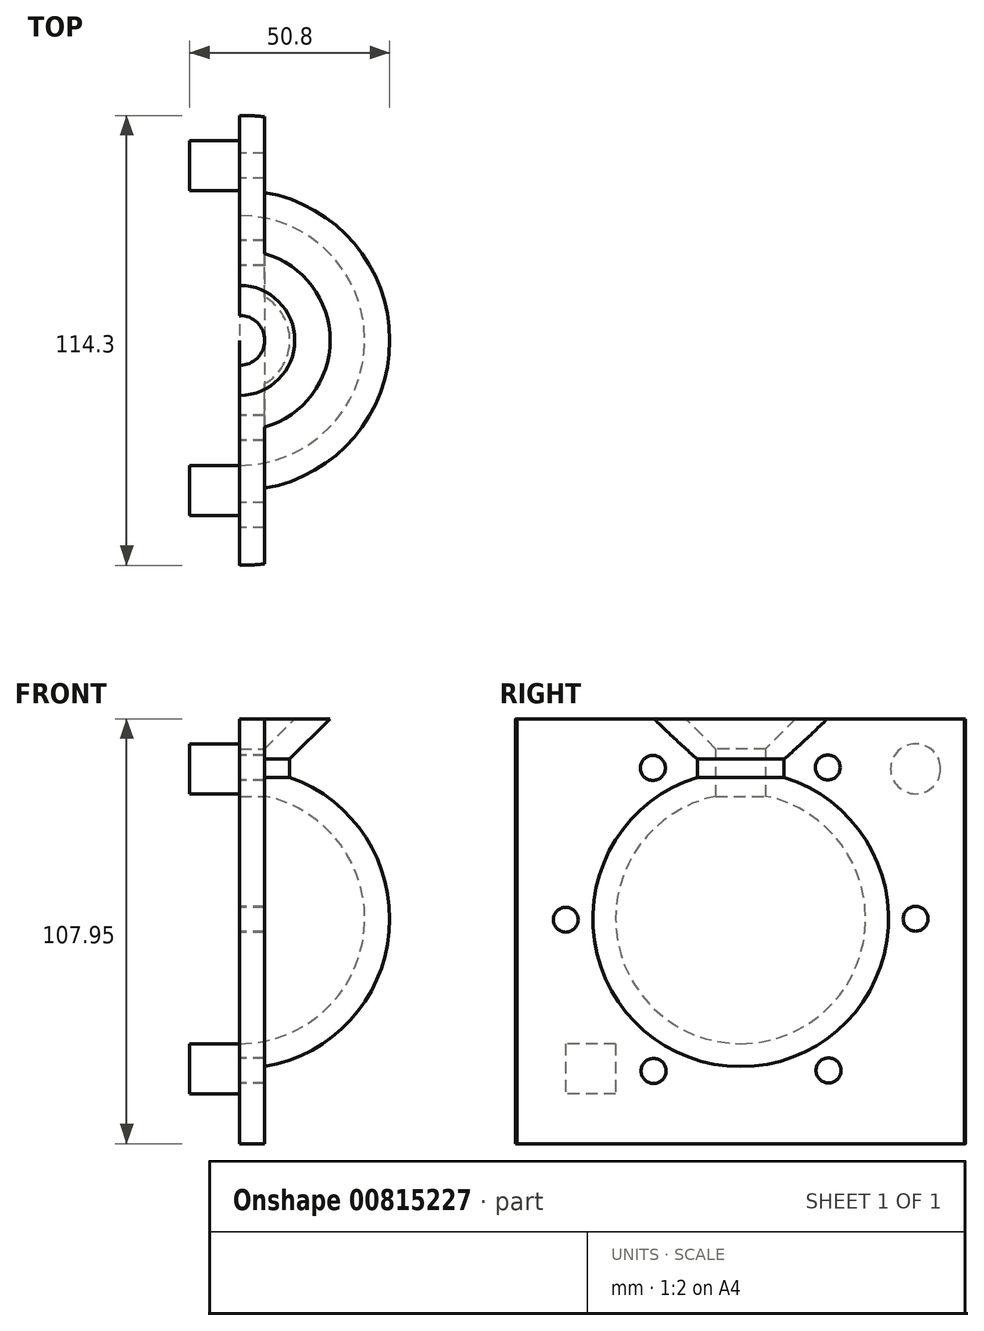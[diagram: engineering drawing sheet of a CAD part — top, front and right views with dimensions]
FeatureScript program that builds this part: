
annotation { "Feature Type Name" : "Feature", "Feature Type Description" : "" }
export const myFeature = defineFeature(function(context is Context, id is Id, definition is map)
    precondition{}
    {
        {
            var Q0;
            Q0=qCreatedBy(makeId("Right.planeOp"),FACE);
            var sketch = newSketch(context, id + "F0", { "sketchPlane" : qUnion([Q0])});
            skCircle(sketch, "E0", {"center": v(0, 0) * mm, "radius": 31.75 * mm});
            skLineSegment(sketch, "E1", {"start": v(0, -31.75) * mm, "end": v(0, -57.15) * mm});
            skLineSegment(sketch, "E2", {"start": v(0, -57.15) * mm, "end": v(57.15, -57.15) * mm});
            skLineSegment(sketch, "E3", {"start": v(57.15, -57.15) * mm, "end": v(57.15, 50.8) * mm});
            skLineSegment(sketch, "E4", {"start": v(57.15, 50.8) * mm, "end": v(6.35, 50.8) * mm});
            skLineSegment(sketch, "E5", {"start": v(6.35, 50.8) * mm, "end": v(6.35, 31.1) * mm});
            skSolve(sketch);
        }
        {
            var Q0;
            {var subQ0=sQuery(id+"F0.wireOp",EDGE,"E1");Q0=makeQuery(id+"F0.imprint","IMPRINT",FACE,{"disambiguationData":[TD([[makeQuery(id+"F0.imprint","IMPRINT",EDGE,{"derivedFrom":subQ0}),1.0]])]});}
            var Q1;
            Q1=sQuery(id+"F0.wireOp",EDGE,"E1");
            revolve(context, id + "F1", {"surfaceOperationType" : NewSurfaceOperationType.NEW, "entities" : qUnion([Q0]), "axis" : qUnion([Q1]), "revolveType" : RevolveType.ONE_DIRECTION, "angle" : 180 * degree});
        }
        {
            var Q0;
            Q0=makeQuery(id+"F1.opRevolve","CAP_FACE",FACE,{"disambiguationData":[OSD([sQuery(id+"F0.wireOp",EDGE,"E0"),sQuery(id+"F0.wireOp",EDGE,"E1"),sQuery(id+"F0.wireOp",EDGE,"E2"),sQuery(id+"F0.wireOp",EDGE,"E3"),sQuery(id+"F0.wireOp",EDGE,"E4"),sQuery(id+"F0.wireOp",EDGE,"E5")])],"isStart":false});
            var sketch = newSketch(context, id + "F2", { "sketchPlane" : qUnion([Q0])});
            skCircle(sketch, "E6", {"center": v(-44.45, 38.1) * mm, "radius": 6.35 * mm});
            skLineSegment(sketch, "E7.bottom", {"start": v(31.75, -31.75) * mm, "end": v(44.45, -31.75) * mm});
            skLineSegment(sketch, "E7.top", {"start": v(31.75, -44.45) * mm, "end": v(44.45, -44.45) * mm});
            skLineSegment(sketch, "E7.left", {"start": v(31.75, -31.75) * mm, "end": v(31.75, -44.45) * mm});
            skLineSegment(sketch, "E7.right", {"start": v(44.45, -31.75) * mm, "end": v(44.45, -44.45) * mm});
            skSolve(sketch);
        }
        {
            var Q0;
            Q0=qSketchRegion(id+"F2",true);
            extrude(context, id + "F3", {"entities" : qUnion([Q0]), "operationType" : NewBodyOperationType.ADD, "depth" : 12.7 * mm, "offsetDistance" : 25.4 * mm});
        }
        {
            var Q0;
            Q0=makeQuery(id+"F1.opRevolve","SWEPT_EDGE",EDGE,{"disambiguationData":[OSD([sQuery(id+"F0.wireOp",EDGE,"E4"),sQuery(id+"F0.wireOp",EDGE,"E5")])]});
            chamfer(context, id + "F4", {"entities" : qUnion([Q0]), "width" : 7.62 * mm, "tangentPropagation" : true});
        }
        {
            var Q0;
            Q0=makeQuery(id+"F1.opRevolve","SWEPT_FACE",FACE,{"disambiguationData":[OSD([sQuery(id+"F0.wireOp",EDGE,"E4")])]});
            var Q1;
            Q1=makeQuery(id+"F1.opRevolve","SWEPT_FACE",FACE,{"disambiguationData":[OSD([sQuery(id+"F0.wireOp",EDGE,"E3")])]});
            var Q2;
            Q2=makeQuery(id+"F1.opRevolve","SWEPT_FACE",FACE,{"disambiguationData":[OSD([sQuery(id+"F0.wireOp",EDGE,"E2")])]});
            shell(context, id + "F5", {"entities" : qUnion([Q0, Q1, Q2]), "thickness" : 6.35 * mm});
        }
        {
            var Q0;
            {var subQ0=sQuery(id+"F0.wireOp",EDGE,"E0");var subQ1=makeQuery(id+"F0.imprint","INTERSECT",VERTEX,{"derivedFrom":[subQ0,sQuery(id+"F0.wireOp",EDGE,"E1")]});Q0=makeQuery(id+"F0.imprint","IMPRINT",FACE,{"disambiguationData":[TD([[makeQuery(id+"F0.imprint","IMPRINT",EDGE,{"disambiguationData":[TD([[subQ1,1.0]])],"derivedFrom":subQ0}),1.0]])]});}
            var sketch = newSketch(context, id + "F6", { "sketchPlane" : qUnion([Q0])});
            skArc(sketch, "E8", {"start": v(24.87, 36.84) * mm, "mid": v(22.18, 38.52) * mm, "end": v(19.37, 40) * mm});
            skCircle(sketch, "E9", {"center": v(44.45, 0) * mm, "radius": 3.18 * mm});
            skCircle(sketch, "E10.1.0", {"center": v(22.12, 38.43) * mm, "radius": 3.18 * mm});
            skCircle(sketch, "E10.2.0", {"center": v(-22.32, 38.3) * mm, "radius": 3.18 * mm});
            skCircle(sketch, "E10.3.0", {"center": v(-44.44, -0.24) * mm, "radius": 3.18 * mm});
            skCircle(sketch, "E10.4.0", {"center": v(-22.11, -38.67) * mm, "radius": 3.18 * mm});
            skCircle(sketch, "E10.5.0", {"center": v(22.33, -38.55) * mm, "radius": 3.18 * mm});
            skPoint(sketch, "E10.center", {"position": v(0, -0.12) * mm});
            skArc(sketch, "E11.trimOffspring", {"start": v(-19.58, 39.9) * mm, "mid": v(-22.38, 38.4) * mm, "end": v(-25.07, 36.7) * mm});
            skArc(sketch, "E12.trimOffspring", {"start": v(-44.35, 2.93) * mm, "mid": v(-44.45, -0.24) * mm, "end": v(-44.32, -3.42) * mm});
            skArc(sketch, "E13.trimOffspring", {"start": v(-24.76, -36.92) * mm, "mid": v(-22.06, -38.59) * mm, "end": v(-19.26, -40.06) * mm});
            skArc(sketch, "E14.trimOffspring", {"start": v(19.48, -39.95) * mm, "mid": v(22.28, -38.46) * mm, "end": v(24.97, -36.78) * mm});
            skArc(sketch, "E15.trimOffspring", {"start": v(44.34, -3.17) * mm, "mid": v(44.45, 0) * mm, "end": v(44.34, 3.17) * mm});
            skSolve(sketch);
        }
        {
            var Q0;
            Q0=qSketchRegion(id+"F6",true);
            extrude(context, id + "F7", {"entities" : qUnion([Q0]), "operationType" : NewBodyOperationType.REMOVE, "oppositeDirection" : true, "depth" : -12.7 * mm, "offsetDistance" : 25.4 * mm});
        }
    });
